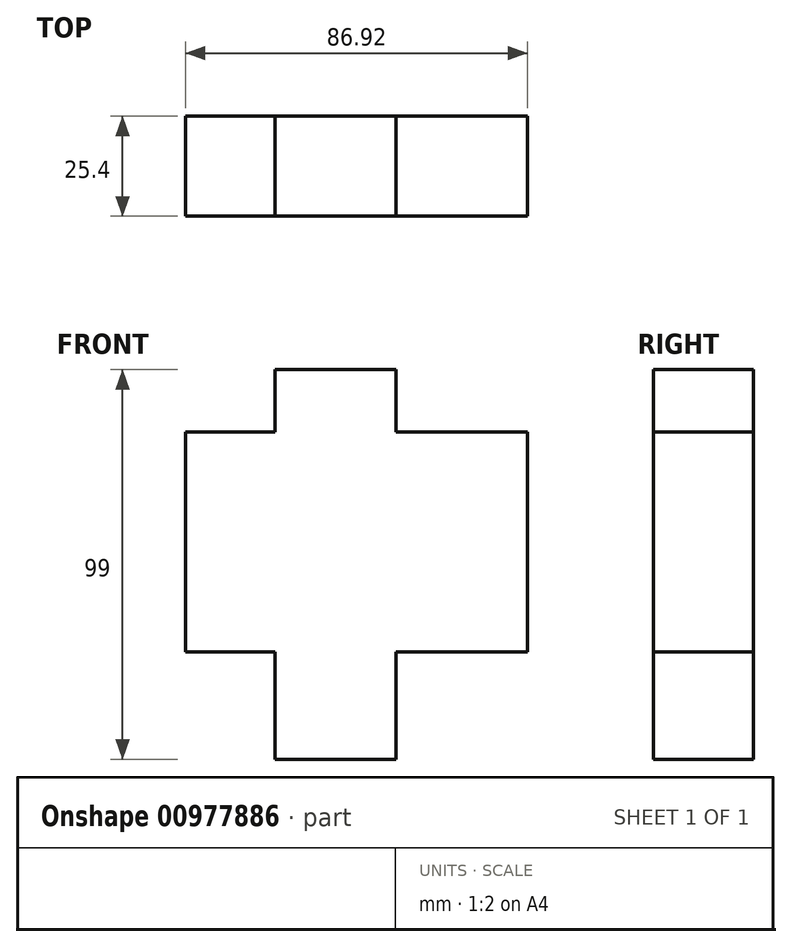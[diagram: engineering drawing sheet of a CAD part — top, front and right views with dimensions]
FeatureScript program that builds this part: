
annotation { "Feature Type Name" : "Feature", "Feature Type Description" : "" }
export const myFeature = defineFeature(function(context is Context, id is Id, definition is map)
    precondition{}
    {
        {
            var Q0;
            Q0=qCreatedBy(makeId("Front.planeOp"),FACE);
            var sketch = newSketch(context, id + "F0", { "sketchPlane" : qUnion([Q0])});
            skLineSegment(sketch, "E0.bottom", {"start": v(-38.42, 19.71) * mm, "end": v(48.5, 19.71) * mm});
            skLineSegment(sketch, "E0.top", {"start": v(-38.42, -36.12) * mm, "end": v(48.5, -36.12) * mm});
            skLineSegment(sketch, "E0.left", {"start": v(-38.42, 19.71) * mm, "end": v(-38.42, -36.12) * mm});
            skLineSegment(sketch, "E0.right", {"start": v(48.5, 19.71) * mm, "end": v(48.5, -36.12) * mm});
            skSolve(sketch);
        }
        {
            var Q0;
            Q0=makeQuery(id+"F0.imprint","IMPRINT",FACE,{"disambiguationData":[TD([[makeQuery(id+"F0.imprint","IMPRINT",EDGE,{"derivedFrom":sQuery(id+"F0.wireOp",EDGE,"E0.bottom")}),-1.0]])]});
            extrude(context, id + "F1", {"entities" : qUnion([Q0]), "depth" : 25.4 * mm, "offsetDistance" : 25.4 * mm});
        }
        {
            var Q0;
            Q0 = qSketchRegion(id + "F0", true);
            extrude(context, id + "F2", {"entities" : qUnion([Q0]), "operationType" : NewBodyOperationType.ADD, "depth" : 25.4 * mm, "offsetDistance" : 25.4 * mm});
        }
        {
            var Q0;
            Q0=qCreatedBy(makeId("Front.planeOp"),FACE);
            var sketch = newSketch(context, id + "F3", { "sketchPlane" : qUnion([Q0])});
            skLineSegment(sketch, "E1.bottom", {"start": v(15.1, 35.54) * mm, "end": v(-15.69, 35.54) * mm});
            skLineSegment(sketch, "E1.top", {"start": v(15.1, -63.46) * mm, "end": v(-15.69, -63.46) * mm});
            skLineSegment(sketch, "E1.left", {"start": v(15.1, 35.54) * mm, "end": v(15.1, -63.46) * mm});
            skLineSegment(sketch, "E1.right", {"start": v(-15.69, 35.54) * mm, "end": v(-15.69, -63.46) * mm});
            skSolve(sketch);
        }
        {
            var Q0;
            Q0 = qSketchRegion(id + "F3", true);
            extrude(context, id + "F4", {"entities" : qUnion([Q0]), "operationType" : NewBodyOperationType.ADD, "depth" : 25.4 * mm, "offsetDistance" : 25.4 * mm});
        }
    });
